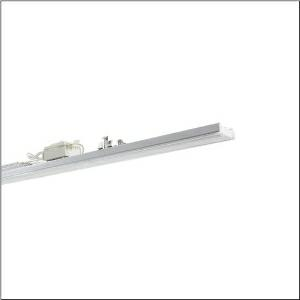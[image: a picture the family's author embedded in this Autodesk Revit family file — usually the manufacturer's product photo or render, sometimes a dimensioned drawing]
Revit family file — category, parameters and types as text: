
# Revit family: licross_11_recessed_mo_51te18cn49xg
name_source: partatom
category: Lighting Fixtures
units: mm (PartAtom-declared; Revit-internal decimal feet)

## family parameters
Cut with Voids When Loaded = No
Host = Face
Light Source = No
Part Type = Normal
Room Calculation Point = No
Round Connector Dimension = Use Diameter
Shared = No

## types (1)
- --- (1 x LED, 9040 lm, 49.3 W, 4000K)
    Apparent Load = 49 VA
    CIE Flux Codes = 83 96 99 100 100
    Color Rendering = 80
    Color Temperature = 4000K
    Default Elevation = 1800 mm
    Description = Licross 11 Recessed MO, luminaire insert, of sheet steel, galvanised, coil coated, white, length: 1.500mm, width: 66mm, height: 67mm, LED rated luminous flux: 9.040lm, light colour: 840, SDCM (Standard Deviation of Colour Matching)MacAdam ≤ 2 SDCM (initial), control gear: ON/OFF Multilumen, CLOi, with plug, 3-pole, with phase selection, mains connection: 220..240V, AC, 50/60Hz, start of lifetime: 49W, end of service life: 55W, internal wiring halogen-free, primary light control with lens, of plastic, primary optical cover: cover, of PMMA, light emission: direct distribution, primary light characteristic: symmetric, protection rating (complete): IP54, insulation class (complete): insulation class I (protective earthing), certification: CE, ENEC, VDE, UKCA, protection symbol: D if used in an environment with non-conductive dust loads with corresponding accessories, impact resistance: IK06, permissible ambient temperature for indoor applications: -35..+40°C, corresponds to IFS (International Featured Standards) requirements for safety and quality in the food industry, reducing of maximum allowable ambient temperature of 5°C with ceiling mounting, LABS conformity tested according to VDMA 24364:2018-05, The light source and the operating device comply with the requirements of the Ecodesign Regulation (EU) 2019/2020 and are replaceable in accordance with this regulation, packaging unit: 1 piece
    Height = 58 mm
    Lamp = 1 x LED
    Lamp Light Flux = 9040 lm
    Lamp Power = 49.3 W
    Lamp count = 1
    Length = 1500 mm
    Luminous efficacy = 183 lm/W
    Manufacturer = Siteco
    ModVariant = No
    Model = 51TE18CN49XG
    Mounting Place = Ceiling
    Mounting Type = Pendant
    Number of Poles = 1
    OnlyDefault = Yes
    Power Factor = 1
    Product Name = Licross 11 Recessed MO
    Product group = luminaire insert | ceiling pendant
    ProductGroupID = 901
    Protection Class = Protection class I
    Protection Degree = IP 54
    RLX_Detail_Level = 1
    RLX_Emergency_Light_Flux = 0 lm
    RLX_Emergency_Type = 0
    RLX_Emergency_Type_DB = No
    RlxData = <blob elided: 22609 chars, md5=7d1ac680>
    Socket = socket
    Standby Power = 0 W
    System Light Flux = 9040 lm
    System Power = 49 W
    Type Comments = factory setting: luminous flux: 100 % | (A | C | E) | 113 mA
    Type Image = l_1296930.jpg
    URL = http://relux.com
    VarID = @adj_089943
    Voltage = 0 V
    Weight = 0.00 kg
    Width = 66 mm

## geometry (parser evidence)
native form markers: Blend x4, Sweep x10
no freeform markers — native parametric forms only
